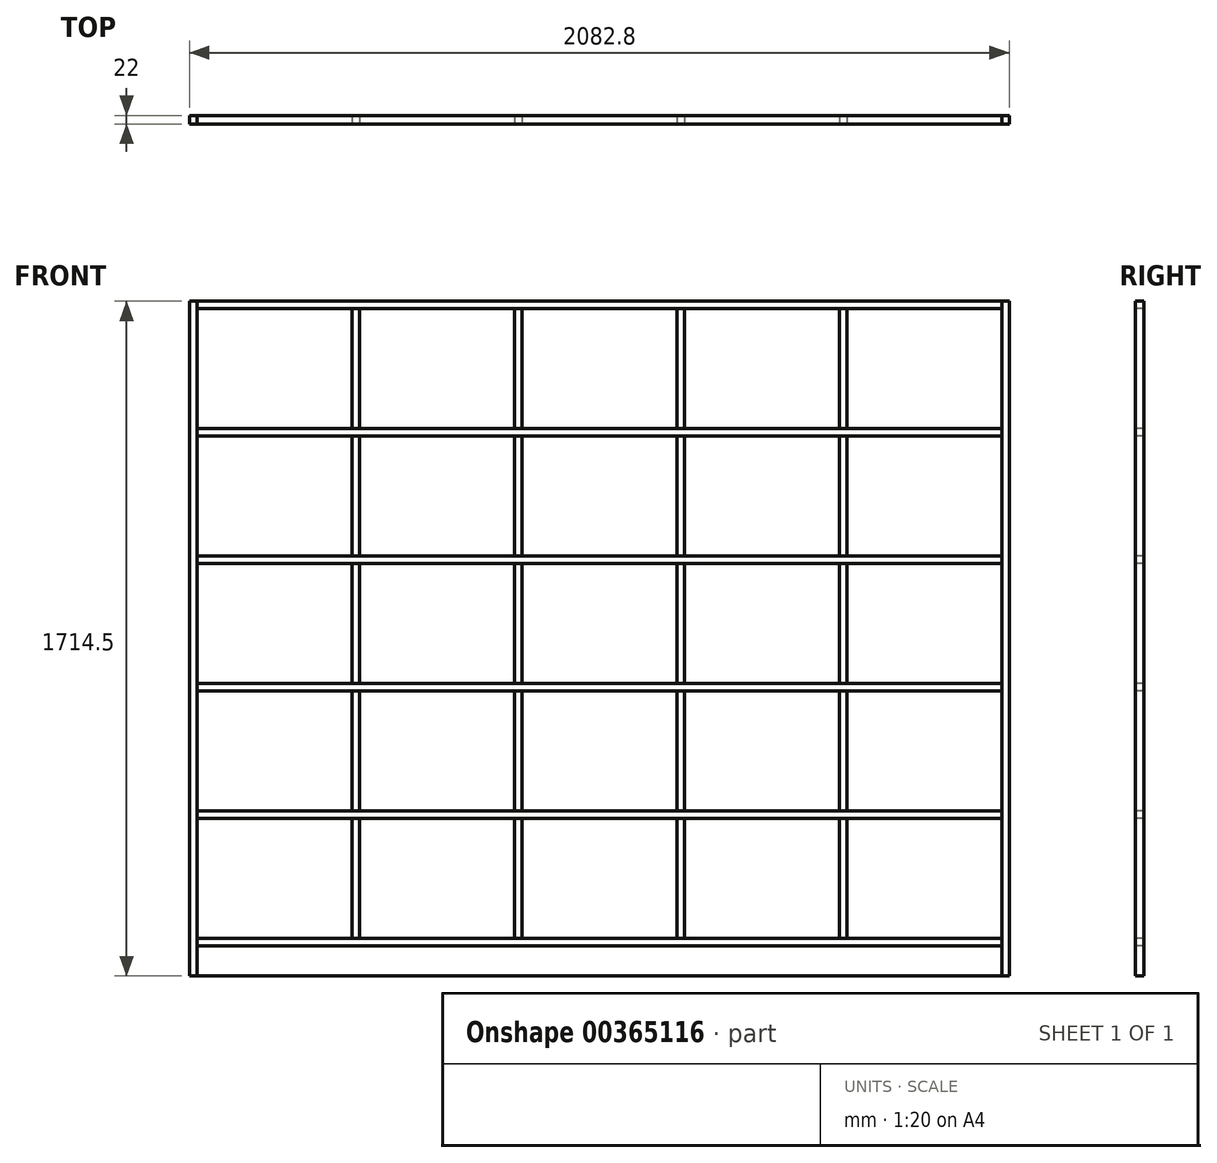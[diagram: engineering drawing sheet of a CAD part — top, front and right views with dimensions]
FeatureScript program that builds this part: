
annotation { "Feature Type Name" : "Feature", "Feature Type Description" : "" }
export const myFeature = defineFeature(function(context is Context, id is Id, definition is map)
    precondition{}
    {
        {
            assignVariable(context, id + "F0", {"name" : "depth", "anyValue" : 22});
        }
        {
            assignVariable(context, id + "F1", {"name" : "plywood", "anyValue" : .75});
        }
        {
            var Q0;
            Q0=qCreatedBy(makeId("Front.planeOp"),FACE);
            var sketch = newSketch(context, id + "F2", { "sketchPlane" : qUnion([Q0])});
            skLineSegment(sketch, "E0", {"start": v(0, 0) * mm, "end": v(0, 1981.2) * mm, "construction": true});
            skLineSegment(sketch, "E1.bottom", {"start": v(-1022.35, 0) * mm, "end": v(1022.35, 0) * mm});
            skLineSegment(sketch, "E1.top", {"start": v(-1022.35, 76.2) * mm, "end": v(1022.35, 76.2) * mm});
            skLineSegment(sketch, "E1.left", {"start": v(-1022.35, 0) * mm, "end": v(-1022.35, 76.2) * mm});
            skLineSegment(sketch, "E1.right", {"start": v(1022.35, 0) * mm, "end": v(1022.35, 76.2) * mm});
            skPoint(sketch, "E1.middle", {"position": v(0, 38.1) * mm});
            skSolve(sketch);
        }
        {
            var Q0;
            Q0=qCreatedBy(makeId("Front.planeOp"),FACE);
            var sketch = newSketch(context, id + "F3", { "sketchPlane" : qUnion([Q0])});
            skLineSegment(sketch, "E2.bottom", {"start": v(-1022.35, 76.2) * mm, "end": v(1022.35, 76.2) * mm});
            skLineSegment(sketch, "E2.top", {"start": v(-1022.35, 95.25) * mm, "end": v(1022.35, 95.25) * mm});
            skLineSegment(sketch, "E2.left", {"start": v(-1022.35, 76.2) * mm, "end": v(-1022.35, 95.25) * mm});
            skLineSegment(sketch, "E2.right", {"start": v(1022.35, 76.2) * mm, "end": v(1022.35, 95.25) * mm});
            skLineSegment(sketch, "E3.0.1.0", {"start": v(-1022.35, 400.05) * mm, "end": v(1022.35, 400.05) * mm});
            skLineSegment(sketch, "E3.0.1.1", {"start": v(-1022.35, 400.05) * mm, "end": v(-1022.35, 419.1) * mm});
            skLineSegment(sketch, "E3.0.1.2", {"start": v(1022.35, 400.05) * mm, "end": v(1022.35, 419.1) * mm});
            skLineSegment(sketch, "E3.0.1.3", {"start": v(-1022.35, 419.1) * mm, "end": v(1022.35, 419.1) * mm});
            skLineSegment(sketch, "E3.0.2.0", {"start": v(-1022.35, 723.9) * mm, "end": v(1022.35, 723.9) * mm});
            skLineSegment(sketch, "E3.0.2.1", {"start": v(-1022.35, 723.9) * mm, "end": v(-1022.35, 742.95) * mm});
            skLineSegment(sketch, "E3.0.2.2", {"start": v(1022.35, 723.9) * mm, "end": v(1022.35, 742.95) * mm});
            skLineSegment(sketch, "E3.0.2.3", {"start": v(-1022.35, 742.95) * mm, "end": v(1022.35, 742.95) * mm});
            skLineSegment(sketch, "E3.0.3.0", {"start": v(-1022.35, 1047.75) * mm, "end": v(1022.35, 1047.75) * mm});
            skLineSegment(sketch, "E3.0.3.1", {"start": v(-1022.35, 1047.75) * mm, "end": v(-1022.35, 1066.8) * mm});
            skLineSegment(sketch, "E3.0.3.2", {"start": v(1022.35, 1047.75) * mm, "end": v(1022.35, 1066.8) * mm});
            skLineSegment(sketch, "E3.0.3.3", {"start": v(-1022.35, 1066.8) * mm, "end": v(1022.35, 1066.8) * mm});
            skLineSegment(sketch, "E3.0.4.0", {"start": v(-1022.35, 1371.6) * mm, "end": v(1022.35, 1371.6) * mm});
            skLineSegment(sketch, "E3.0.4.1", {"start": v(-1022.35, 1371.6) * mm, "end": v(-1022.35, 1390.65) * mm});
            skLineSegment(sketch, "E3.0.4.2", {"start": v(1022.35, 1371.6) * mm, "end": v(1022.35, 1390.65) * mm});
            skLineSegment(sketch, "E3.0.4.3", {"start": v(-1022.35, 1390.65) * mm, "end": v(1022.35, 1390.65) * mm});
            skLineSegment(sketch, "E3.direction1", {"start": v(-1022.35, 76.2) * mm, "end": v(-996.95, 76.2) * mm, "construction": true});
            skLineSegment(sketch, "E3.direction2", {"start": v(-1022.35, 76.2) * mm, "end": v(-1022.35, 400.05) * mm, "construction": true});
            skLineSegment(sketch, "E4.0.0.5", {"start": v(-1022.35, 1695.45) * mm, "end": v(1022.35, 1695.45) * mm});
            skLineSegment(sketch, "E4.3.0.5", {"start": v(-1022.35, 1695.45) * mm, "end": v(-1022.35, 1714.5) * mm});
            skLineSegment(sketch, "E4.6.0.5", {"start": v(1022.35, 1695.45) * mm, "end": v(1022.35, 1714.5) * mm});
            skLineSegment(sketch, "E4.9.0.5", {"start": v(-1022.35, 1714.5) * mm, "end": v(1022.35, 1714.5) * mm});
            skSolve(sketch);
        }
        {
            var Q0;
            Q0=qCreatedBy(makeId("Front.planeOp"),FACE);
            var sketch = newSketch(context, id + "F4", { "sketchPlane" : qUnion([Q0])});
            skLineSegment(sketch, "E5.bottom", {"start": v(-1022.35, 0) * mm, "end": v(-1041.4, 0) * mm});
            skLineSegment(sketch, "E5.top", {"start": v(-1022.35, 1714.5) * mm, "end": v(-1041.4, 1714.5) * mm});
            skLineSegment(sketch, "E5.left", {"start": v(-1022.35, 0) * mm, "end": v(-1022.35, 1714.5) * mm});
            skLineSegment(sketch, "E5.right", {"start": v(-1041.4, 0) * mm, "end": v(-1041.4, 1714.5) * mm});
            skLineSegment(sketch, "E6.bottom", {"start": v(1041.4, 0) * mm, "end": v(1022.35, 0) * mm});
            skLineSegment(sketch, "E6.top", {"start": v(1041.4, 1714.5) * mm, "end": v(1022.35, 1714.5) * mm});
            skLineSegment(sketch, "E6.left", {"start": v(1041.4, 0) * mm, "end": v(1041.4, 1714.5) * mm});
            skLineSegment(sketch, "E6.right", {"start": v(1022.35, 0) * mm, "end": v(1022.35, 1714.5) * mm});
            skSolve(sketch);
        }
        {
            var Q0;
            Q0=qCreatedBy(makeId("Front.planeOp"),FACE);
            var sketch = newSketch(context, id + "F5", { "sketchPlane" : qUnion([Q0])});
            skLineSegment(sketch, "E7.bottom", {"start": v(-628.65, 400.05) * mm, "end": v(-609.6, 400.05) * mm});
            skLineSegment(sketch, "E7.top", {"start": v(-628.65, 95.25) * mm, "end": v(-609.6, 95.25) * mm});
            skLineSegment(sketch, "E7.left", {"start": v(-628.65, 400.05) * mm, "end": v(-628.65, 95.25) * mm});
            skLineSegment(sketch, "E7.right", {"start": v(-609.6, 400.05) * mm, "end": v(-609.6, 95.25) * mm});
            skLineSegment(sketch, "E8.0.1.0", {"start": v(-609.6, 723.9) * mm, "end": v(-609.6, 419.1) * mm});
            skLineSegment(sketch, "E8.0.1.1", {"start": v(-628.65, 723.9) * mm, "end": v(-609.6, 723.9) * mm});
            skLineSegment(sketch, "E8.0.1.2", {"start": v(-628.65, 419.1) * mm, "end": v(-609.6, 419.1) * mm});
            skLineSegment(sketch, "E8.0.1.3", {"start": v(-628.65, 723.9) * mm, "end": v(-628.65, 419.1) * mm});
            skLineSegment(sketch, "E8.0.2.0", {"start": v(-609.6, 1047.75) * mm, "end": v(-609.6, 742.95) * mm});
            skLineSegment(sketch, "E8.0.2.1", {"start": v(-628.65, 1047.75) * mm, "end": v(-609.6, 1047.75) * mm});
            skLineSegment(sketch, "E8.0.2.2", {"start": v(-628.65, 742.95) * mm, "end": v(-609.6, 742.95) * mm});
            skLineSegment(sketch, "E8.0.2.3", {"start": v(-628.65, 1047.75) * mm, "end": v(-628.65, 742.95) * mm});
            skLineSegment(sketch, "E8.0.3.0", {"start": v(-609.6, 1371.6) * mm, "end": v(-609.6, 1066.8) * mm});
            skLineSegment(sketch, "E8.0.3.1", {"start": v(-628.65, 1371.6) * mm, "end": v(-609.6, 1371.6) * mm});
            skLineSegment(sketch, "E8.0.3.2", {"start": v(-628.65, 1066.8) * mm, "end": v(-609.6, 1066.8) * mm});
            skLineSegment(sketch, "E8.0.3.3", {"start": v(-628.65, 1371.6) * mm, "end": v(-628.65, 1066.8) * mm});
            skLineSegment(sketch, "E8.0.4.0", {"start": v(-609.6, 1695.45) * mm, "end": v(-609.6, 1390.65) * mm});
            skLineSegment(sketch, "E8.0.4.1", {"start": v(-628.65, 1695.45) * mm, "end": v(-609.6, 1695.45) * mm});
            skLineSegment(sketch, "E8.0.4.2", {"start": v(-628.65, 1390.65) * mm, "end": v(-609.6, 1390.65) * mm});
            skLineSegment(sketch, "E8.0.4.3", {"start": v(-628.65, 1695.45) * mm, "end": v(-628.65, 1390.65) * mm});
            skLineSegment(sketch, "E8.1.0.0", {"start": v(-196.85, 400.05) * mm, "end": v(-196.85, 95.25) * mm});
            skLineSegment(sketch, "E8.1.0.1", {"start": v(-215.9, 400.05) * mm, "end": v(-196.85, 400.05) * mm});
            skLineSegment(sketch, "E8.1.0.2", {"start": v(-215.9, 95.25) * mm, "end": v(-196.85, 95.25) * mm});
            skLineSegment(sketch, "E8.1.0.3", {"start": v(-215.9, 400.05) * mm, "end": v(-215.9, 95.25) * mm});
            skLineSegment(sketch, "E8.1.1.0", {"start": v(-196.85, 723.9) * mm, "end": v(-196.85, 419.1) * mm});
            skLineSegment(sketch, "E8.1.1.1", {"start": v(-215.9, 723.9) * mm, "end": v(-196.85, 723.9) * mm});
            skLineSegment(sketch, "E8.1.1.2", {"start": v(-215.9, 419.1) * mm, "end": v(-196.85, 419.1) * mm});
            skLineSegment(sketch, "E8.1.1.3", {"start": v(-215.9, 723.9) * mm, "end": v(-215.9, 419.1) * mm});
            skLineSegment(sketch, "E8.1.2.0", {"start": v(-196.85, 1047.75) * mm, "end": v(-196.85, 742.95) * mm});
            skLineSegment(sketch, "E8.1.2.1", {"start": v(-215.9, 1047.75) * mm, "end": v(-196.85, 1047.75) * mm});
            skLineSegment(sketch, "E8.1.2.2", {"start": v(-215.9, 742.95) * mm, "end": v(-196.85, 742.95) * mm});
            skLineSegment(sketch, "E8.1.2.3", {"start": v(-215.9, 1047.75) * mm, "end": v(-215.9, 742.95) * mm});
            skLineSegment(sketch, "E8.1.3.0", {"start": v(-196.85, 1371.6) * mm, "end": v(-196.85, 1066.8) * mm});
            skLineSegment(sketch, "E8.1.3.1", {"start": v(-215.9, 1371.6) * mm, "end": v(-196.85, 1371.6) * mm});
            skLineSegment(sketch, "E8.1.3.2", {"start": v(-215.9, 1066.8) * mm, "end": v(-196.85, 1066.8) * mm});
            skLineSegment(sketch, "E8.1.3.3", {"start": v(-215.9, 1371.6) * mm, "end": v(-215.9, 1066.8) * mm});
            skLineSegment(sketch, "E8.1.4.0", {"start": v(-196.85, 1695.45) * mm, "end": v(-196.85, 1390.65) * mm});
            skLineSegment(sketch, "E8.1.4.1", {"start": v(-215.9, 1695.45) * mm, "end": v(-196.85, 1695.45) * mm});
            skLineSegment(sketch, "E8.1.4.2", {"start": v(-215.9, 1390.65) * mm, "end": v(-196.85, 1390.65) * mm});
            skLineSegment(sketch, "E8.1.4.3", {"start": v(-215.9, 1695.45) * mm, "end": v(-215.9, 1390.65) * mm});
            skLineSegment(sketch, "E8.2.0.0", {"start": v(215.9, 400.05) * mm, "end": v(215.9, 95.25) * mm});
            skLineSegment(sketch, "E8.2.0.1", {"start": v(196.85, 400.05) * mm, "end": v(215.9, 400.05) * mm});
            skLineSegment(sketch, "E8.2.0.2", {"start": v(196.85, 95.25) * mm, "end": v(215.9, 95.25) * mm});
            skLineSegment(sketch, "E8.2.0.3", {"start": v(196.85, 400.05) * mm, "end": v(196.85, 95.25) * mm});
            skLineSegment(sketch, "E8.2.1.0", {"start": v(215.9, 723.9) * mm, "end": v(215.9, 419.1) * mm});
            skLineSegment(sketch, "E8.2.1.1", {"start": v(196.85, 723.9) * mm, "end": v(215.9, 723.9) * mm});
            skLineSegment(sketch, "E8.2.1.2", {"start": v(196.85, 419.1) * mm, "end": v(215.9, 419.1) * mm});
            skLineSegment(sketch, "E8.2.1.3", {"start": v(196.85, 723.9) * mm, "end": v(196.85, 419.1) * mm});
            skLineSegment(sketch, "E8.2.2.0", {"start": v(215.9, 1047.75) * mm, "end": v(215.9, 742.95) * mm});
            skLineSegment(sketch, "E8.2.2.1", {"start": v(196.85, 1047.75) * mm, "end": v(215.9, 1047.75) * mm});
            skLineSegment(sketch, "E8.2.2.2", {"start": v(196.85, 742.95) * mm, "end": v(215.9, 742.95) * mm});
            skLineSegment(sketch, "E8.2.2.3", {"start": v(196.85, 1047.75) * mm, "end": v(196.85, 742.95) * mm});
            skLineSegment(sketch, "E8.2.3.0", {"start": v(215.9, 1371.6) * mm, "end": v(215.9, 1066.8) * mm});
            skLineSegment(sketch, "E8.2.3.1", {"start": v(196.85, 1371.6) * mm, "end": v(215.9, 1371.6) * mm});
            skLineSegment(sketch, "E8.2.3.2", {"start": v(196.85, 1066.8) * mm, "end": v(215.9, 1066.8) * mm});
            skLineSegment(sketch, "E8.2.3.3", {"start": v(196.85, 1371.6) * mm, "end": v(196.85, 1066.8) * mm});
            skLineSegment(sketch, "E8.2.4.0", {"start": v(215.9, 1695.45) * mm, "end": v(215.9, 1390.65) * mm});
            skLineSegment(sketch, "E8.2.4.1", {"start": v(196.85, 1695.45) * mm, "end": v(215.9, 1695.45) * mm});
            skLineSegment(sketch, "E8.2.4.2", {"start": v(196.85, 1390.65) * mm, "end": v(215.9, 1390.65) * mm});
            skLineSegment(sketch, "E8.2.4.3", {"start": v(196.85, 1695.45) * mm, "end": v(196.85, 1390.65) * mm});
            skLineSegment(sketch, "E8.3.0.0", {"start": v(628.65, 400.05) * mm, "end": v(628.65, 95.25) * mm});
            skLineSegment(sketch, "E8.3.0.1", {"start": v(609.6, 400.05) * mm, "end": v(628.65, 400.05) * mm});
            skLineSegment(sketch, "E8.3.0.2", {"start": v(609.6, 95.25) * mm, "end": v(628.65, 95.25) * mm});
            skLineSegment(sketch, "E8.3.0.3", {"start": v(609.6, 400.05) * mm, "end": v(609.6, 95.25) * mm});
            skLineSegment(sketch, "E8.3.1.0", {"start": v(628.65, 723.9) * mm, "end": v(628.65, 419.1) * mm});
            skLineSegment(sketch, "E8.3.1.1", {"start": v(609.6, 723.9) * mm, "end": v(628.65, 723.9) * mm});
            skLineSegment(sketch, "E8.3.1.2", {"start": v(609.6, 419.1) * mm, "end": v(628.65, 419.1) * mm});
            skLineSegment(sketch, "E8.3.1.3", {"start": v(609.6, 723.9) * mm, "end": v(609.6, 419.1) * mm});
            skLineSegment(sketch, "E8.3.2.0", {"start": v(628.65, 1047.75) * mm, "end": v(628.65, 742.95) * mm});
            skLineSegment(sketch, "E8.3.2.1", {"start": v(609.6, 1047.75) * mm, "end": v(628.65, 1047.75) * mm});
            skLineSegment(sketch, "E8.3.2.2", {"start": v(609.6, 742.95) * mm, "end": v(628.65, 742.95) * mm});
            skLineSegment(sketch, "E8.3.2.3", {"start": v(609.6, 1047.75) * mm, "end": v(609.6, 742.95) * mm});
            skLineSegment(sketch, "E8.3.3.0", {"start": v(628.65, 1371.6) * mm, "end": v(628.65, 1066.8) * mm});
            skLineSegment(sketch, "E8.3.3.1", {"start": v(609.6, 1371.6) * mm, "end": v(628.65, 1371.6) * mm});
            skLineSegment(sketch, "E8.3.3.2", {"start": v(609.6, 1066.8) * mm, "end": v(628.65, 1066.8) * mm});
            skLineSegment(sketch, "E8.3.3.3", {"start": v(609.6, 1371.6) * mm, "end": v(609.6, 1066.8) * mm});
            skLineSegment(sketch, "E8.3.4.0", {"start": v(628.65, 1695.45) * mm, "end": v(628.65, 1390.65) * mm});
            skLineSegment(sketch, "E8.3.4.1", {"start": v(609.6, 1695.45) * mm, "end": v(628.65, 1695.45) * mm});
            skLineSegment(sketch, "E8.3.4.2", {"start": v(609.6, 1390.65) * mm, "end": v(628.65, 1390.65) * mm});
            skLineSegment(sketch, "E8.3.4.3", {"start": v(609.6, 1695.45) * mm, "end": v(609.6, 1390.65) * mm});
            skLineSegment(sketch, "E8.direction1", {"start": v(-628.65, 95.25) * mm, "end": v(-215.9, 95.25) * mm, "construction": true});
            skLineSegment(sketch, "E8.direction2", {"start": v(-628.65, 95.25) * mm, "end": v(-628.65, 419.1) * mm, "construction": true});
            skSolve(sketch);
        }
        {
            var Q0;
            Q0 = qSketchRegion(id + "F2", true);
            extrude(context, id + "F6", {"entities" : qUnion([Q0]), "oppositeDirection" : true, "depth" : (getVariable(context, 'plywood')) * mm});
        }
        {
            var Q0;
            Q0 = qSketchRegion(id + "F2", true);
            extrude(context, id + "F7", {"entities" : qUnion([Q0]), "oppositeDirection" : true, "depth" : (getVariable(context, 'depth')) * mm, "hasSecondDirection" : true, "secondDirectionOppositeDirection" : true, "secondDirectionDepth" : ((getVariable(context, 'depth')) - (getVariable(context, 'plywood'))) * mm});
        }
        {
            var Q0;
            Q0 = qSketchRegion(id + "F3", true);
            extrude(context, id + "F8", {"entities" : qUnion([Q0]), "oppositeDirection" : true, "depth" : (getVariable(context, 'depth')) * mm});
        }
        {
            var Q0;
            Q0 = qSketchRegion(id + "F4", true);
            extrude(context, id + "F9", {"entities" : qUnion([Q0]), "oppositeDirection" : true, "depth" : (getVariable(context, 'depth')) * mm});
        }
        {
            var Q0;
            Q0 = qSketchRegion(id + "F5", true);
            extrude(context, id + "F10", {"entities" : qUnion([Q0]), "oppositeDirection" : true, "depth" : (getVariable(context, 'depth')) * mm});
        }
    });
